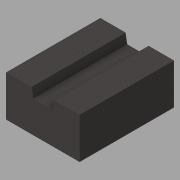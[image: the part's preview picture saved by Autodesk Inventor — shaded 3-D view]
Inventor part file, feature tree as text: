
AUTODESK INVENTOR PART (.ipt)
format: ipt  version: 2018 (Build 220112000, 112)  size: 100,352 bytes
history: native  units: in
note: dims shown in document units (in); Inventor stores cm internally (conversion verified against a paired STEP export)
features: extrude x1, sketch x1
ambient origin geometry x8: Origin, YZ Plane, XZ Plane, XY Plane, X Axis, Y Axis, Z Axis, Center Point
bodies: Solid1 (feature_tree)
feature tree (2):
  extrude  "Extrusion1"  Depth=360.0in
  sketch  "Sketch1"  dims[d0=96.0in d1=76.0in d2=36.0in d3=0.6871in d4=0.6871in d5=120.0in d7=360.0in d8=0.0in]
